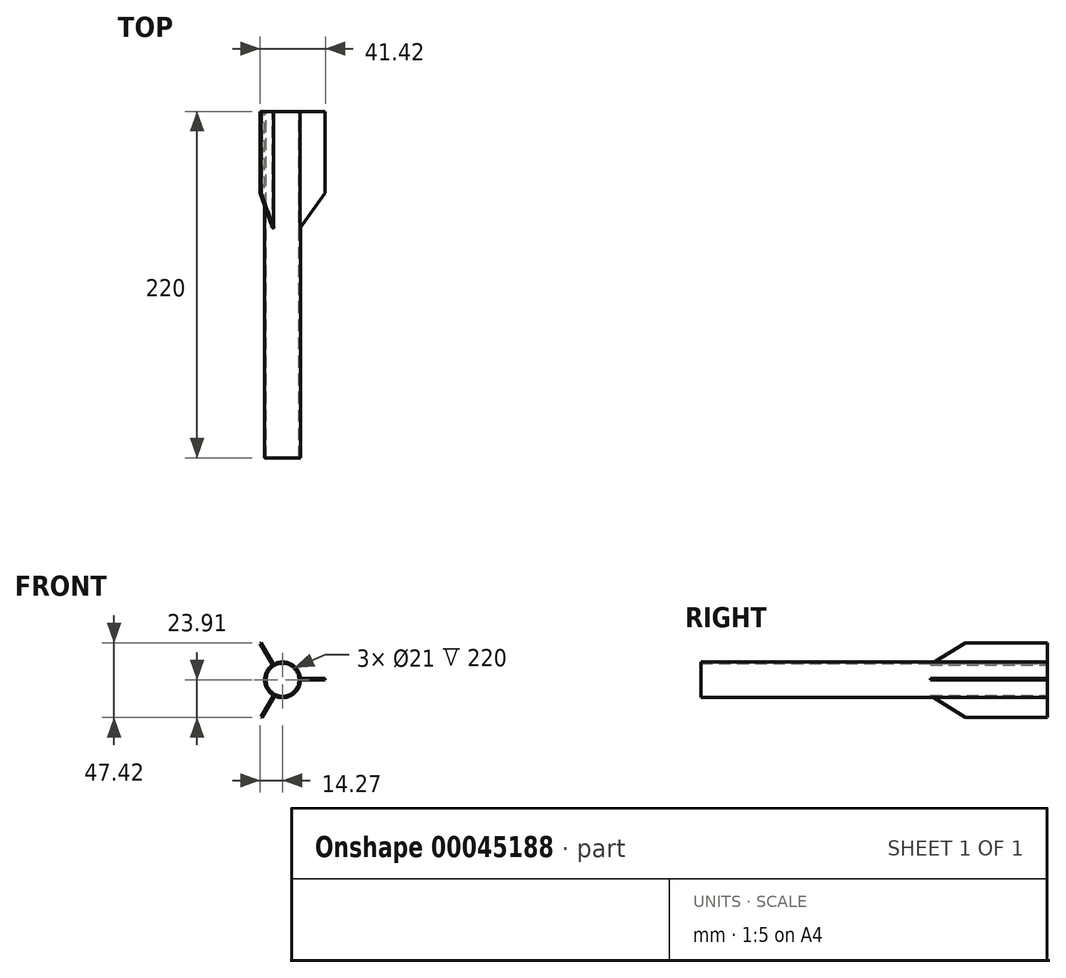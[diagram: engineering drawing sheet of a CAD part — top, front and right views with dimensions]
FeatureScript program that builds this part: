
annotation { "Feature Type Name" : "Feature", "Feature Type Description" : "" }
export const myFeature = defineFeature(function(context is Context, id is Id, definition is map)
    precondition{}
    {
        {
            var Q0;
            Q0=qCreatedBy(makeId("Front.planeOp"),FACE);
            var sketch = newSketch(context, id + "F0", { "sketchPlane" : qUnion([Q0])});
            skCircle(sketch, "E0", {"center": v(0, 0) * mm, "radius": 10.5 * mm});
            skCircle(sketch, "E1", {"center": v(0, 0) * mm, "radius": 11.3 * mm});
            skSolve(sketch);
        }
        {
            var Q0;
            Q0=makeQuery(id+"F0.imprint","IMPRINT",FACE,{"disambiguationData":[TD([[makeQuery(id+"F0.imprint","IMPRINT",EDGE,{"derivedFrom":sQuery(id+"F0.wireOp",EDGE,"E0")}),-1.0]])]});
            extrude(context, id + "F1", {"entities" : qUnion([Q0]), "depth" : 220 * mm});
        }
        {
            var Q0;
            Q0=qCreatedBy(makeId("Top.planeOp"),FACE);
            var sketch = newSketch(context, id + "F2", { "sketchPlane" : qUnion([Q0])});
            skLineSegment(sketch, "E2", {"start": v(10.8, -74.8) * mm, "end": v(10.8, 0) * mm});
            skLineSegment(sketch, "E3", {"start": v(10.8, 0) * mm, "end": v(27.15, 0) * mm});
            skLineSegment(sketch, "E4", {"start": v(27.15, 0) * mm, "end": v(27.15, -51.85) * mm});
            skLineSegment(sketch, "E5", {"start": v(27.15, -51.85) * mm, "end": v(10.8, -74.8) * mm});
            skSolve(sketch);
        }
        {
            var Q0;
            Q0=makeQuery(id+"F2.imprint","IMPRINT",FACE,{"disambiguationData":[TD([[makeQuery(id+"F2.imprint","IMPRINT",EDGE,{"derivedFrom":sQuery(id+"F2.wireOp",EDGE,"E2")}),-1.0]])]});
            extrude(context, id + "F3", {"entities" : qUnion([Q0]), "operationType" : NewBodyOperationType.ADD, "depth" : 0.8 * mm});
        }
        {
            var Q0;
            Q0=makeQuery(id+"F1.opExtrude","SWEPT_BODY",BODY,{"disambiguationData":[OSD([sQuery(id+"F0.wireOp",EDGE,"E0"),sQuery(id+"F0.wireOp",EDGE,"E1")])]});
            var Q1;
            Q1=makeQuery(id+"F1.opExtrude","SWEPT_FACE",FACE,{"disambiguationData":[OSD([sQuery(id+"F0.wireOp",EDGE,"E1")])]});
            circularPattern(context, id + "F4", {"entities" : qUnion([Q0]), "axis" : qUnion([Q1]), "angle" : 360 * degree, "instanceCount" : 3, "equalSpace" : true});
        }
    });
